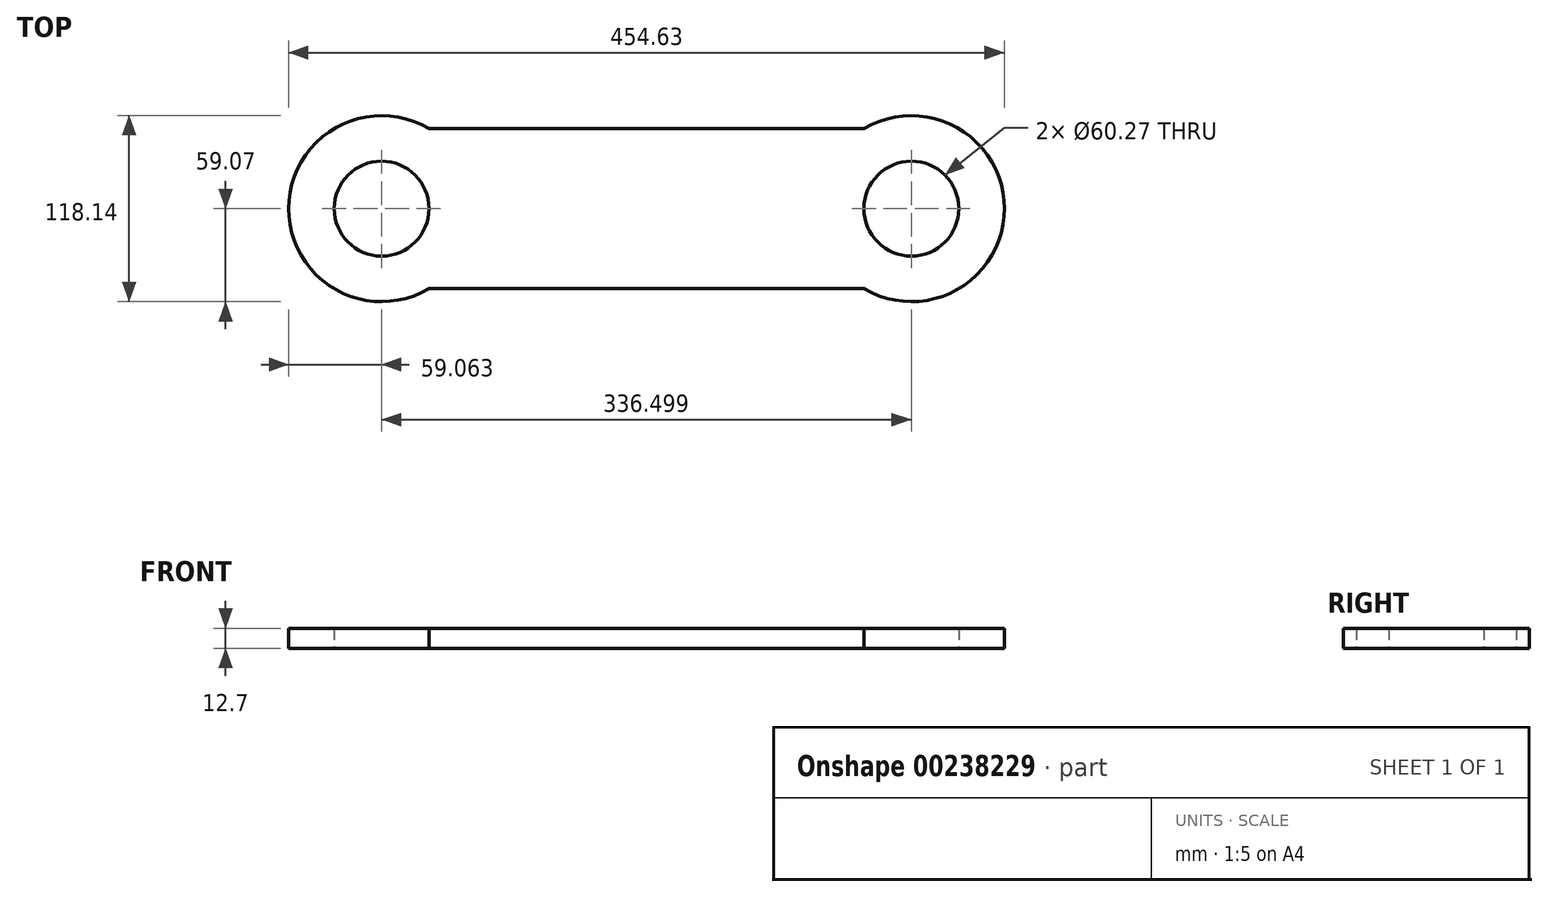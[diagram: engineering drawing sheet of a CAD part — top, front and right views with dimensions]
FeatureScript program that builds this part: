
annotation { "Feature Type Name" : "Feature", "Feature Type Description" : "" }
export const myFeature = defineFeature(function(context is Context, id is Id, definition is map)
    precondition{}
    {
        {
            var Q0;
            Q0=qCreatedBy(makeId("Top.planeOp"),FACE);
            var sketch = newSketch(context, id + "F0", { "sketchPlane" : qUnion([Q0])});
            skLineSegment(sketch, "E0.bottom", {"start": v(0, 0) * mm, "end": v(276.23, 0) * mm});
            skLineSegment(sketch, "E0.top", {"start": v(0, 101.6) * mm, "end": v(276.23, 101.6) * mm});
            skLineSegment(sketch, "E1", {"start": v(0, 50.8) * mm, "end": v(-30.14, 50.8) * mm});
            skPoint(sketch, "E1.endSnap0", {"position": v(0, 50.8) * mm});
            skLineSegment(sketch, "E2", {"start": v(276.23, 50.8) * mm, "end": v(306.36, 50.8) * mm});
            skCircle(sketch, "E3", {"center": v(306.36, 50.8) * mm, "radius": 30.14 * mm});
            skCircle(sketch, "E4", {"center": v(-30.14, 50.8) * mm, "radius": 30.14 * mm});
            skArc(sketch, "E5", {"start": v(276.23, 0) * mm, "mid": v(365.43, 50.8) * mm, "end": v(276.23, 101.6) * mm});
            skArc(sketch, "E6", {"start": v(0, 101.6) * mm, "mid": v(-89.2, 50.8) * mm, "end": v(0, 0) * mm});
            skSolve(sketch);
        }
        {
            var Q0;
            Q0=makeQuery(id+"F0.imprint","IMPRINT",FACE,{"disambiguationData":[TD([[makeQuery(id+"F0.imprint","IMPRINT",EDGE,{"derivedFrom":sQuery(id+"F0.wireOp",EDGE,"E0.bottom")}),1.0]])]});
            extrude(context, id + "F1", {"entities" : qUnion([Q0]), "depth" : 12.7 * mm});
        }
    });
